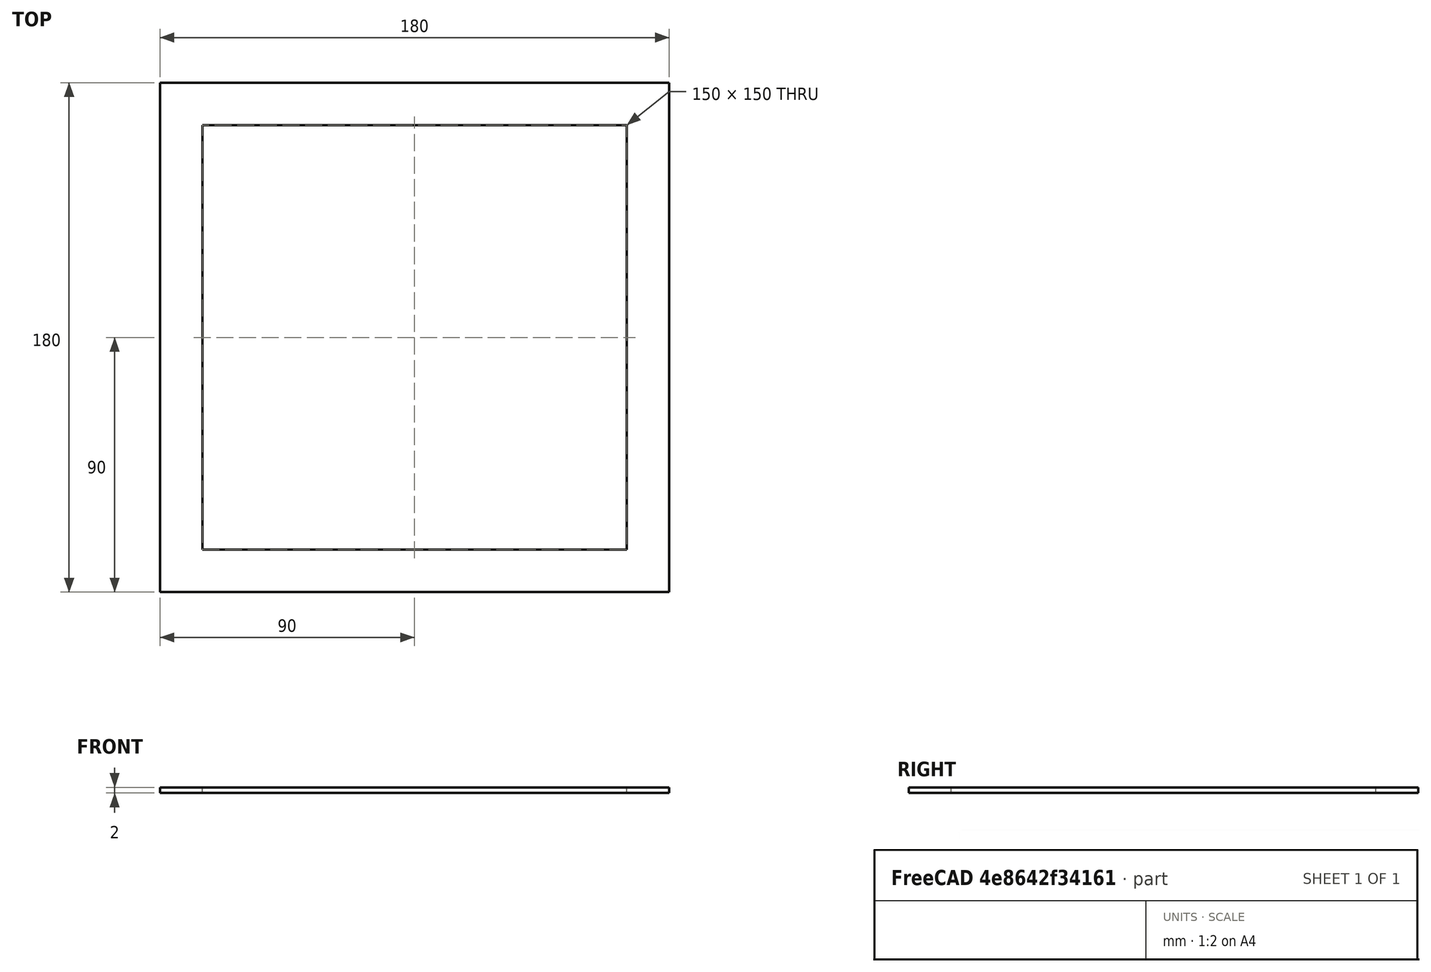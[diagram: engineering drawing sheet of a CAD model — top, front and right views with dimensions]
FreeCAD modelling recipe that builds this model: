
FCSTD DOCUMENT  (FreeCAD 1.0R38806 (Git))
Label: Frame75Holder
License: All rights reserved
LicenseURL: https://en.wikipedia.org/wiki/All_rights_reserved
objects: PartDesign::Plane×1, Sketcher::SketchObject×1, PartDesign::Pad×1, PartDesign::Body×1
note: 7 computed .brp shape members not serialized (recipe doc carries the construction recipe); baked Part::Feature solids carry a one-line shape summary decoded from their .brp

FEATURE [PartDesign::Plane] DatumPlane
  AttachmentSupport = -> [XY_Plane]
  Length = 60
  MapMode = 5
  ResizeMode = 0
  Width = 60
FEATURE [Sketcher::SketchObject] Sketch  label="FrameBaseS"
  ArcFitTolerance = 0
  AttachmentOffset = pos=(0,0,-2) rot=(0,0,1;0rad)
  AttachmentSupport = -> [DatumPlane]
  FullyConstrained = true
  MakeInternals = false
  MapMode = 5
  Placement = pos=(0,0,-2) rot=(0,0,1;0rad)
  sketch-geometry (10):
    g0: LineSegment StartX=-90 StartY=-90 StartZ=0 EndX=-90 EndY=90 EndZ=0
    g1: LineSegment StartX=-90 StartY=90 StartZ=0 EndX=90 EndY=90 EndZ=0
    g2: LineSegment StartX=90 StartY=90 StartZ=0 EndX=90 EndY=-90 EndZ=0
    g3: LineSegment StartX=90 StartY=-90 StartZ=0 EndX=-90 EndY=-90 EndZ=0
    g4: GeomPoint [constr] X=0 Y=0 Z=0
    g5: LineSegment StartX=-75 StartY=-75 StartZ=0 EndX=-75 EndY=75 EndZ=0
    g6: LineSegment StartX=-75 StartY=75 StartZ=0 EndX=75 EndY=75 EndZ=0
    g7: LineSegment StartX=75 StartY=75 StartZ=0 EndX=75 EndY=-75 EndZ=0
    g8: LineSegment StartX=75 StartY=-75 StartZ=0 EndX=-75 EndY=-75 EndZ=0
    g9: GeomPoint [constr] X=0 Y=0 Z=0
  constraints (24):
    c: Coincident(g0,g1)
    c: Coincident(g1,g2)
    c: Coincident(g2,g3)
    c: Coincident(g3,g0)
    c: Horizontal(g1)
    c: Horizontal(g3)
    c: Vertical(g0)
    c: Vertical(g2)
    c: Symmetric(g1,g0,g4)
    c: Coincident(g4,g-1)
    c: DistanceY(g0,g0) = 180  'Frame Height'
    c: DistanceX(g1,g1) = 180  'Frame Width'
    c: Coincident(g5,g6)
    c: Coincident(g6,g7)
    c: Coincident(g7,g8)
    c: Coincident(g8,g5)
    c: Horizontal(g6)
    c: Horizontal(g8)
    c: Vertical(g5)
    c: Vertical(g7)
    c: Symmetric(g6,g5,g9)
    c: Coincident(g9,g4)
    c: Distance(g5,g0) = 15
    c: Distance(g1,g6) = 15
FEATURE [PartDesign::Pad] Pad  label="FrameBase"
  Direction = (0,0,1)
  Length = 2
  Length2 = 10
  Profile = -> Sketch
  ReferenceAxis = -> Sketch [N_Axis]
  Suppressed = false
  Type = 0
FEATURE [PartDesign::Body] Body  label="FrameHolder"
  AllowCompound = false
  Group = -> [DatumPlane,Sketch,Pad]
  Origin = -> Origin
  Tip = -> Pad
